# Revit family: BRILLOSA DINAMICA 48V RGB_SL4814W.RGB
name_source: partatom
category: Luminarias
units: mm (PartAtom-declared; Revit-internal decimal feet)

## family parameters
Compartido = No
Corte con vacíos al cargar = No
Cota de conector redondo = Diámetro de uso
Origen de luz = Sí
Punto de cálculo de habitación = No
Se basa en plano de trabajo = Sí
Siempre vertical = No
Tipo de pieza = Normal

## types (1)
- BRILLOSA DINAMICA 48V RGB_SL4814W.RGB
    Cambio de temperatura de color de luz atenuada = <Ninguno>
    Comentarios de vataje = 48
    Descripción = TIRA BRILLOSA DINAMICA RGB DE UN MATERIAL PCB BLANCO MONTADA EN UNA CINTA ADHERIBLE 3M, CON UNA POTENCIA DE 15W/M DE UN TIPO DE LED 5050 SMD, USO PARA EXTERIORES IP20, 300 LUMENES POR METRO, PRESENTACION DE 40M, CORTE 16.6CM, AMPERAJE 0.28A, ALIMENTADO A 48V, REQUIERE ACCESORIOS.
    Elevación por defecto = 0 mm  [stored 0 ft]
    Fabricante = BRILLANT
    Filtro de color = 16777215
    Longitud de línea de emisión = 600 mm
    Marca = BRILLANT
    Modelo = SL4814W.RGB
    Modelo Lampara = 5050 SMD
    Tamaño de símbolo de origen de luz = 610 mm

note: [stored X ft] marks values corroborated as IEEE doubles in the binary element streams (Revit-internal decimal feet)

## geometry (parser evidence)
native form markers: Blend x2
no freeform markers — native parametric forms only
